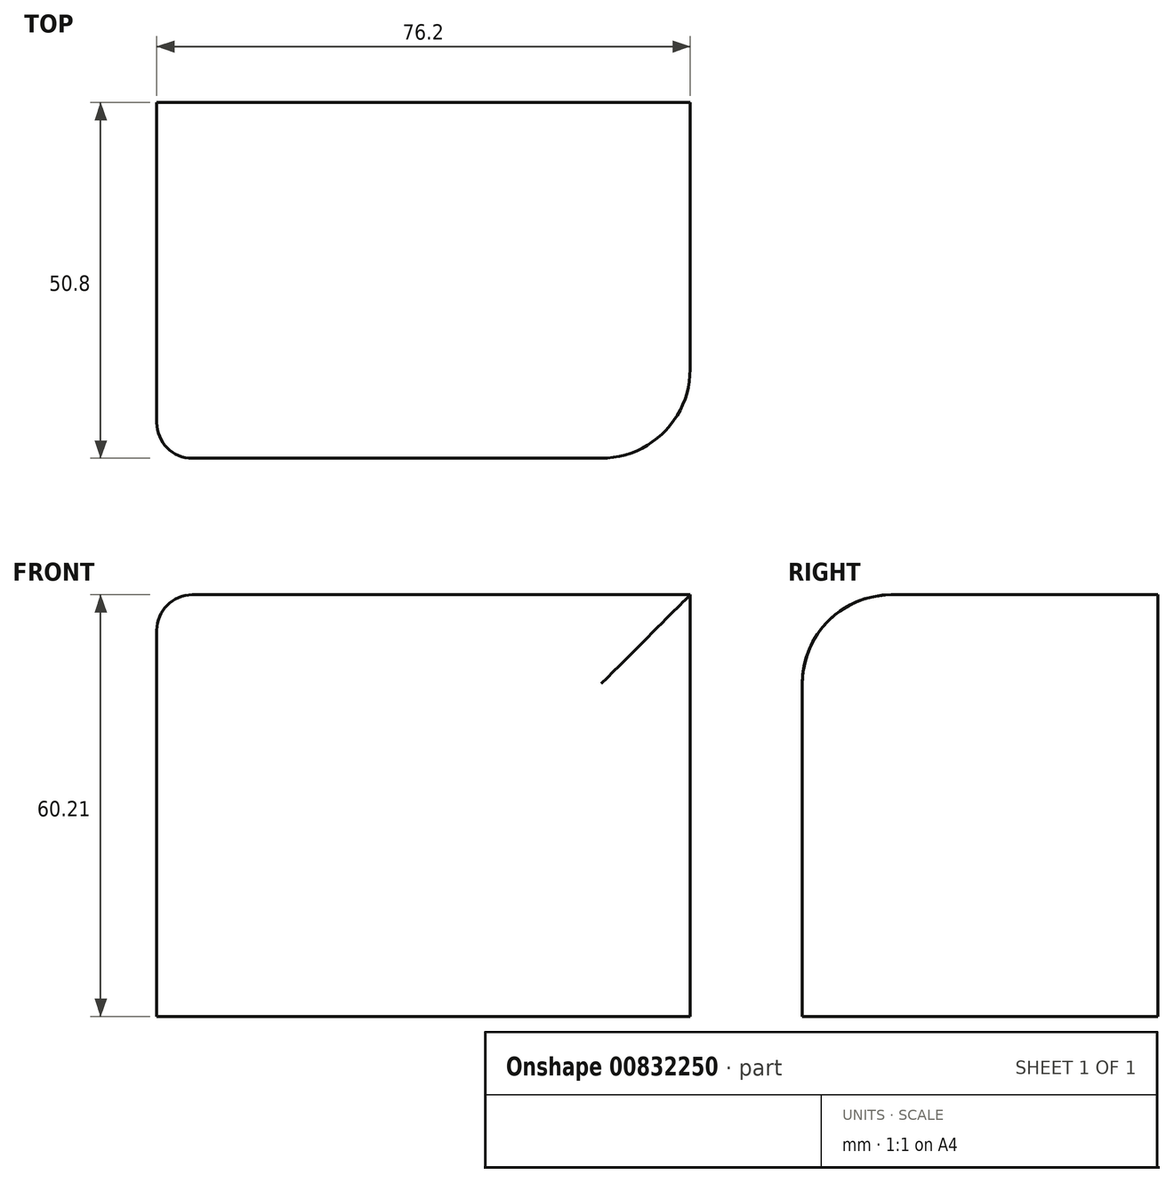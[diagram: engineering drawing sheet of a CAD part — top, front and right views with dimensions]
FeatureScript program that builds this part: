
annotation { "Feature Type Name" : "Feature", "Feature Type Description" : "" }
export const myFeature = defineFeature(function(context is Context, id is Id, definition is map)
    precondition{}
    {
        {
            var Q0;
            Q0=qCreatedBy(makeId("Front.planeOp"),FACE);
            var sketch = newSketch(context, id + "F0", { "sketchPlane" : qUnion([Q0])});
            skLineSegment(sketch, "E0.bottom", {"start": v(-72.28, 60.2) * mm, "end": v(3.92, 60.2) * mm});
            skLineSegment(sketch, "E0.top", {"start": v(-72.28, 0) * mm, "end": v(3.92, 0) * mm});
            skLineSegment(sketch, "E0.left", {"start": v(-72.28, 60.2) * mm, "end": v(-72.28, 0) * mm});
            skLineSegment(sketch, "E0.right", {"start": v(3.92, 60.2) * mm, "end": v(3.92, 0) * mm});
            skLineSegment(sketch, "E1.bottom", {"start": v(3.92, 0) * mm, "end": v(3.92, 0) * mm});
            skLineSegment(sketch, "E1.top", {"start": v(3.92, 0) * mm, "end": v(3.92, 0) * mm});
            skLineSegment(sketch, "E1.left", {"start": v(3.92, 0) * mm, "end": v(3.92, 0) * mm});
            skLineSegment(sketch, "E1.right", {"start": v(3.92, 0) * mm, "end": v(3.92, 0) * mm});
            skSolve(sketch);
        }
        {
            var Q0;
            Q0=makeQuery(id+"F0.imprint","IMPRINT",FACE,{"disambiguationData":[TD([[makeQuery(id+"F0.imprint","IMPRINT",EDGE,{"derivedFrom":sQuery(id+"F0.wireOp",EDGE,"E0.bottom")}),-1.0]])]});
            extrude(context, id + "F1", {"entities" : qUnion([Q0]), "depth" : 50.8 * mm, "offsetDistance" : 25.4 * mm});
        }
        {
            var Q0;
            Q0=makeQuery(id+"F1.opExtrude","CAP_EDGE",EDGE,{"disambiguationData":[OSD([sQuery(id+"F0.wireOp",EDGE,"E0.bottom")])],"isStart":false});
            var Q1;
            Q1=makeQuery(id+"F1.opExtrude","CAP_EDGE",EDGE,{"disambiguationData":[OSD([sQuery(id+"F0.wireOp",EDGE,"E0.right")])],"isStart":false});
            fillet(context, id + "F2", {"entities" : qUnion([Q0, Q1]), "radius" : 12.7 * mm, "tangentPropagation" : true, "allowEdgeOverflow" : false});
        }
        {
            var Q0;
            Q0=makeQuery(id+"F1.opExtrude","CAP_EDGE",EDGE,{"disambiguationData":[OSD([sQuery(id+"F0.wireOp",EDGE,"E0.left")])],"isStart":false});
            fillet(context, id + "F3", {"entities" : qUnion([Q0]), "radius" : 5.08 * mm, "tangentPropagation" : true, "allowEdgeOverflow" : false});
        }
    });
